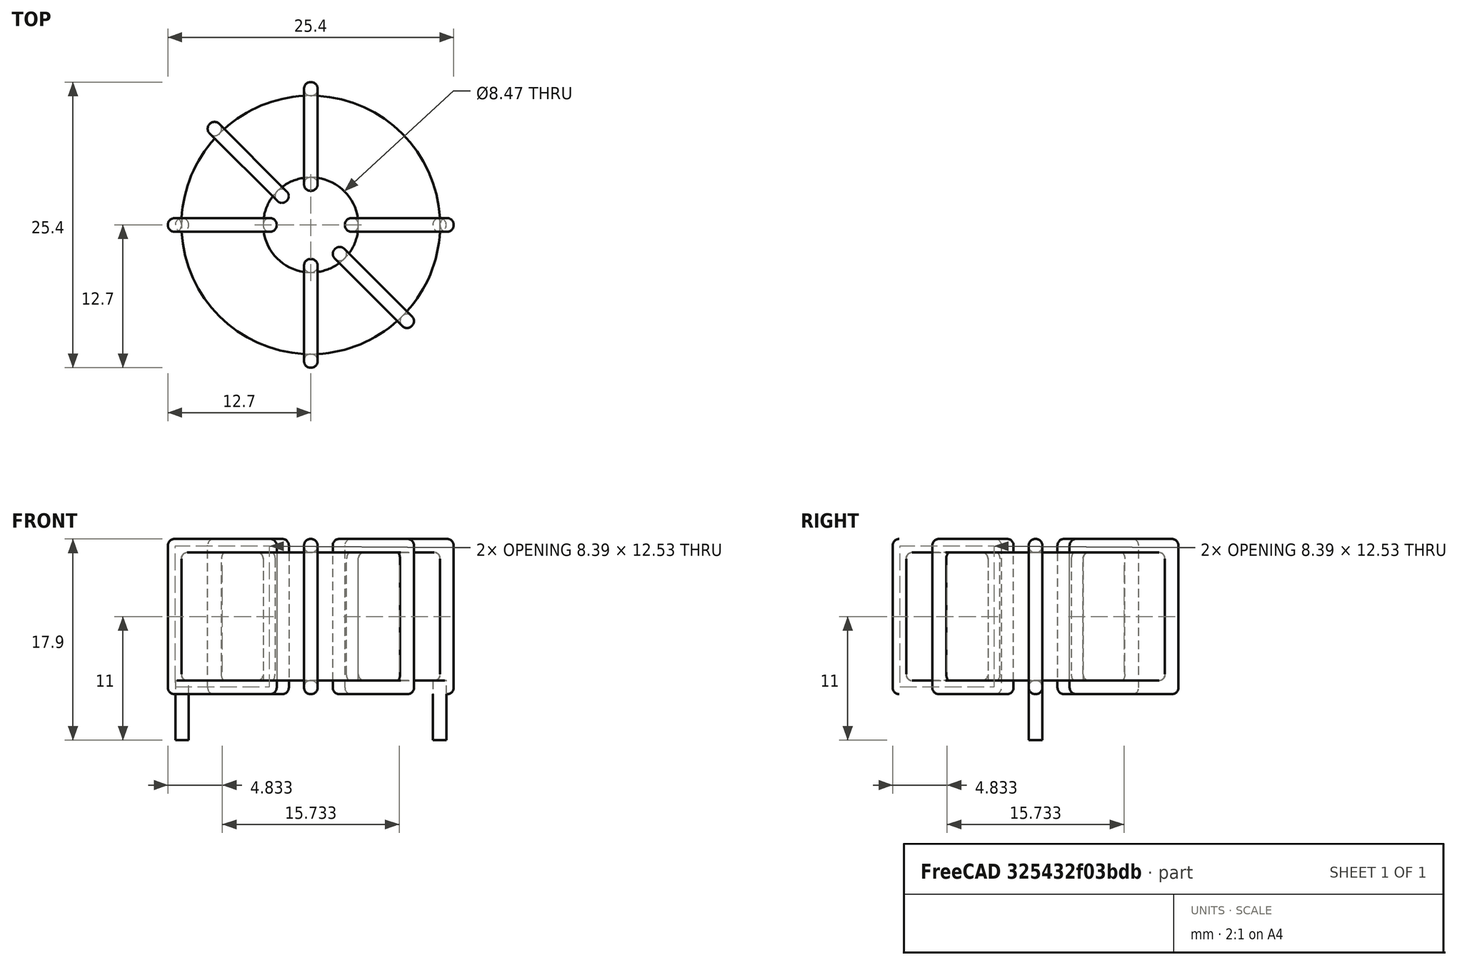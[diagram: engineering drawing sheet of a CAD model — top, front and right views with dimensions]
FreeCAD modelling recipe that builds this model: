
FCSTD DOCUMENT  (FreeCAD 0.16R6703 (Git))
Label: L_Toroid_Horizontal_D25.4mm_P22.90mm_Vishay_TJ5_BigPads
License: All rights reserved
LicenseURL: http://en.wikipedia.org/wiki/All_rights_reserved
objects: Sketcher::SketchObject×6, PartDesign::Pad×6, PartDesign::Fillet×5, Spreadsheet::Sheet×1
note: 23 computed .brp shape members not serialized (recipe doc carries the construction recipe); baked Part::Feature solids carry a one-line shape summary decoded from their .brp

FEATURE [Spreadsheet::Sheet] Spreadsheet  label="dimensions"
  cells = A1=Wx; B1(Wx)=25.4; C1(WW)=8.466666666666667; D1=25.4; A2=Wy; B2(Wy)=25.4; D2=25.4; A3=RM; B3(RMx)=22.9; C3(RMy)=0; A4=d_wire; B4(d_wire)=1.2; A5=H; B5(H)=11.4; A6=offsetx; B6(offsetx)=1.25
FEATURE [Sketcher::SketchObject] Sketch
  Placement = pos=(0,0,1.7) rot=(0,0,1;0rad)
  expr: Placement.Base.z = 0.5 + Spreadsheet.d_wire
  expr: Constraints[0] = Spreadsheet.Wx / 2 - Spreadsheet.d_wire
  expr: Constraints[4] = Spreadsheet.WW / 2
  expr: Constraints[2] = Spreadsheet.RMy / 2
  expr: Constraints[1] = Spreadsheet.RMx / 2
  sketch-geometry (2):
    g0: Circle CenterX=11.45 CenterY=0 CenterZ=0 NormalX=0 NormalY=0 NormalZ=1 Radius=11.5
    g1: Circle CenterX=11.45 CenterY=0 CenterZ=0 NormalX=0 NormalY=0 NormalZ=1 Radius=4.23333
  constraints (5):
    c: Radius(g0) = 11.5
    c: DistanceX(g-1,g0) = 11.45
    c: DistanceY(g-1,g0) = 0
    c: Coincident(g1,g0)
    c: Radius(g1) = 4.23333
FEATURE [PartDesign::Pad] Pad
  Length = 11.4
  Length2 = 100
  Placement = pos=(0,0,1.7) rot=(0,0,1;0rad)
  Sketch = -> Sketch
  Type = 0
  expr: Length = Spreadsheet.H
FEATURE [Sketcher::SketchObject] Sketch001
  Placement = pos=(0,0,1.1) rot=(0,0,1;0rad)
  expr: Placement.Base.z = 0.5 + Spreadsheet.d_wire * 0.5
  expr: Constraints[4] = Spreadsheet.RMx
  expr: Constraints[2] = Spreadsheet.RMy
  expr: Constraints[1] = Spreadsheet.d_wire / 2
  sketch-geometry (2):
    g0: Circle CenterX=0 CenterY=0 CenterZ=0 NormalX=0 NormalY=0 NormalZ=1 Radius=0.6
    g1: Circle CenterX=22.9 CenterY=0 CenterZ=0 NormalX=0 NormalY=0 NormalZ=1 Radius=0.6
  constraints (5):
    c: Equal(g0,g1)
    c: Radius(g0) = 0.6
    c: DistanceY(g-1,g1) = 0
    c: Coincident(g0,g-1)
    c: DistanceX(g-1,g1) = 22.9
FEATURE [PartDesign::Pad] Pad001
  Length = 0.6
  Length2 = 4.7
  Placement = pos=(0,0,1.1) rot=(0,0,1;0rad)
  Reversed = true
  Sketch = -> Sketch001
  Type = 4
  expr: Length2 = 3.5 + Spreadsheet.d_wire
  expr: Length = Spreadsheet.d_wire / 2
FEATURE [PartDesign::Fillet] Fillet
  Base = -> Pad [Edge6,Edge3,Edge2]
  Placement = pos=(0,0,1.7) rot=(0,0,1;0rad)
  Radius = 0.5
FEATURE [Sketcher::SketchObject] Sketch003
  Placement = pos=(11.45,0,0) rot=(1,0,0;1.5708rad)
  expr: Placement.Base.x = Spreadsheet.RMx / 2
  expr: Constraints[49] = Spreadsheet.Wx - Spreadsheet.d_wire * 2
  expr: Constraints[44] = Spreadsheet.d_wire
  expr: Constraints[23] = Spreadsheet.H
  expr: Constraints[22] = Spreadsheet.Wx / 2 - Spreadsheet.d_wire
  expr: Placement.Base.y = Spreadsheet.RMy / 2
  expr: Constraints[21] = (Spreadsheet.Wx - Spreadsheet.WW) / 2 - Spreadsheet.d_wire
  expr: Constraints[19] = Spreadsheet.d_wire
  expr: Constraints[17] = Spreadsheet.d_wire
  expr: Constraints[18] = Spreadsheet.d_wire
  expr: Constraints[16] = Spreadsheet.d_wire
  sketch-geometry (16):
    g0: LineSegment StartX=-3.03333 StartY=0.5 StartZ=0 EndX=-12.7 EndY=0.5 EndZ=0
    g1: LineSegment StartX=-12.7 StartY=0.5 StartZ=0 EndX=-12.7 EndY=14.3 EndZ=0
    g2: LineSegment StartX=-12.7 StartY=14.3 StartZ=0 EndX=-3.03333 EndY=14.3 EndZ=0
    g3: LineSegment StartX=-3.03333 StartY=14.3 StartZ=0 EndX=-3.03333 EndY=0.5 EndZ=0
    g4: LineSegment StartX=-11.5 StartY=13.1 StartZ=0 EndX=-4.23333 EndY=13.1 EndZ=0
    g5: LineSegment StartX=-4.23333 StartY=13.1 StartZ=0 EndX=-4.23333 EndY=1.7 EndZ=0
    g6: LineSegment StartX=-4.23333 StartY=1.7 StartZ=0 EndX=-11.5 EndY=1.7 EndZ=0
    g7: LineSegment StartX=-11.5 StartY=1.7 StartZ=0 EndX=-11.5 EndY=13.1 EndZ=0
    g8: LineSegment StartX=3.03333 StartY=14.3 StartZ=0 EndX=12.7 EndY=14.3 EndZ=0
    g9: LineSegment StartX=12.7 StartY=14.3 StartZ=0 EndX=12.7 EndY=0.5 EndZ=0
    g10: LineSegment StartX=12.7 StartY=0.5 StartZ=0 EndX=3.03333 EndY=0.5 EndZ=0
    g11: LineSegment StartX=3.03333 StartY=0.5 StartZ=0 EndX=3.03333 EndY=14.3 EndZ=0
    g12: LineSegment StartX=4.23333 StartY=13.1 StartZ=0 EndX=11.5 EndY=13.1 EndZ=0
    g13: LineSegment StartX=11.5 StartY=13.1 StartZ=0 EndX=11.5 EndY=1.7 EndZ=0
    g14: LineSegment StartX=11.5 StartY=1.7 StartZ=0 EndX=4.23333 EndY=1.7 EndZ=0
    g15: LineSegment StartX=4.23333 StartY=1.7 StartZ=0 EndX=4.23333 EndY=13.1 EndZ=0
  constraints (50):
    c: Horizontal(g0)
    c: Coincident(g1,g0)
    c: Vertical(g1)
    c: Coincident(g2,g1)
    c: Horizontal(g2)
    c: Coincident(g3,g2)
    c: Coincident(g3,g0)
    c: Vertical(g3)
    c: Coincident(g4,g5)
    c: Coincident(g5,g6)
    c: Coincident(g6,g7)
    c: Coincident(g7,g4)
    c: Horizontal(g4)
    c: Horizontal(g6)
    c: Vertical(g5)
    c: Vertical(g7)
    c: DistanceX(g1,g4) = 1.2
    c: DistanceY(g4,g1) = 1.2
    c: DistanceX(g5,g0) = 1.2
    c: DistanceY(g0,g5) = 1.2
    c: DistanceY(g-1,g0) = 0.5
    c: DistanceX(g6,g6) = 7.26667
    c: DistanceX(g6,g-1) = 11.5
    c: DistanceY(g7,g7) = 11.4
    c: Coincident(g8,g9)
    c: Coincident(g9,g10)
    c: Coincident(g10,g11)
    c: Coincident(g11,g8)
    c: Horizontal(g8)
    c: Horizontal(g10)
    c: Vertical(g9)
    c: Vertical(g11)
    c: Coincident(g12,g13)
    c: Coincident(g13,g14)
    c: Coincident(g14,g15)
    c: Coincident(g15,g12)
    c: Horizontal(g12)
    c: Horizontal(g14)
    c: Vertical(g13)
    c: Vertical(g15)
    c: DistanceY(g8,g2) = 0
    c: DistanceY(g10,g0) = 0
    c: DistanceY(g14,g5) = 0
    c: DistanceY(g12,g4) = 0
    c: DistanceX(g8,g12) = 1.2
    c: Equal(g8,g2)
    c: Equal(g12,g4)
    c: Equal(g9,g1)
    c: Equal(g13,g7)
    c: DistanceX(g4,g12) = 23
FEATURE [PartDesign::Pad] Pad002
  Length = 1.2
  Length2 = 100
  Midplane = true
  Placement = pos=(11.45,0,0) rot=(1,0,0;1.5708rad)
  Sketch = -> Sketch003
  Type = 0
  expr: Length = Spreadsheet.d_wire
FEATURE [PartDesign::Fillet] Fillet001
  Base = -> Pad002 [Edge38,Edge41,Edge42,Edge43,Edge29,Edge32,Edge33,Edge34,Edge25,Edge35,Edge36,Edge13,Edge14,Edge15,Edge16,Edge17,Edge18,Edge19,Edge1,Edge2,Edge3,Edge4,Edge5,Edge6,Edge7,Edge37,Edge39,Edge40,Edge20,Edge23,Edge24,Edge21,Edge22,Edge8,Edge9,Edge10,Edge11,Edge12,Edge26,Edge27,+8 more]
  Placement = pos=(11.45,0,0) rot=(1,0,0;1.5708rad)
  Radius = 0.564
  expr: Radius = Spreadsheet.d_wire * 0.47
FEATURE [Sketcher::SketchObject] Sketch004
  Placement = pos=(11.45,0,0) rot=(0.862856,0.357407,0.357407;1.71777rad)
  expr: Placement.Base.x = Spreadsheet.RMx / 2
  expr: Constraints[49] = Spreadsheet.Wx - 2 * Spreadsheet.d_wire
  expr: Constraints[44] = Spreadsheet.d_wire
  expr: Constraints[23] = Spreadsheet.H
  expr: Constraints[22] = Spreadsheet.Wx / 2 - Spreadsheet.d_wire
  expr: Placement.Base.y = Spreadsheet.RMy / 2
  expr: Constraints[21] = (Spreadsheet.Wx - Spreadsheet.WW) / 2 - Spreadsheet.d_wire
  expr: Constraints[19] = Spreadsheet.d_wire
  expr: Constraints[17] = Spreadsheet.d_wire
  expr: Constraints[18] = Spreadsheet.d_wire
  expr: Constraints[16] = Spreadsheet.d_wire
  sketch-geometry (16):
    g0: LineSegment StartX=-3.03333 StartY=0.5 StartZ=0 EndX=-12.7 EndY=0.5 EndZ=0
    g1: LineSegment StartX=-12.7 StartY=0.5 StartZ=0 EndX=-12.7 EndY=14.3 EndZ=0
    g2: LineSegment StartX=-12.7 StartY=14.3 StartZ=0 EndX=-3.03333 EndY=14.3 EndZ=0
    g3: LineSegment StartX=-3.03333 StartY=14.3 StartZ=0 EndX=-3.03333 EndY=0.5 EndZ=0
    g4: LineSegment StartX=-11.5 StartY=13.1 StartZ=0 EndX=-4.23333 EndY=13.1 EndZ=0
    g5: LineSegment StartX=-4.23333 StartY=13.1 StartZ=0 EndX=-4.23333 EndY=1.7 EndZ=0
    g6: LineSegment StartX=-4.23333 StartY=1.7 StartZ=0 EndX=-11.5 EndY=1.7 EndZ=0
    g7: LineSegment StartX=-11.5 StartY=1.7 StartZ=0 EndX=-11.5 EndY=13.1 EndZ=0
    g8: LineSegment StartX=3.03333 StartY=14.3 StartZ=0 EndX=12.7 EndY=14.3 EndZ=0
    g9: LineSegment StartX=12.7 StartY=14.3 StartZ=0 EndX=12.7 EndY=0.5 EndZ=0
    g10: LineSegment StartX=12.7 StartY=0.5 StartZ=0 EndX=3.03333 EndY=0.5 EndZ=0
    g11: LineSegment StartX=3.03333 StartY=0.5 StartZ=0 EndX=3.03333 EndY=14.3 EndZ=0
    g12: LineSegment StartX=4.23333 StartY=13.1 StartZ=0 EndX=11.5 EndY=13.1 EndZ=0
    g13: LineSegment StartX=11.5 StartY=13.1 StartZ=0 EndX=11.5 EndY=1.7 EndZ=0
    g14: LineSegment StartX=11.5 StartY=1.7 StartZ=0 EndX=4.23333 EndY=1.7 EndZ=0
    g15: LineSegment StartX=4.23333 StartY=1.7 StartZ=0 EndX=4.23333 EndY=13.1 EndZ=0
  constraints (50):
    c: Horizontal(g0)
    c: Coincident(g1,g0)
    c: Vertical(g1)
    c: Coincident(g2,g1)
    c: Horizontal(g2)
    c: Coincident(g3,g2)
    c: Coincident(g3,g0)
    c: Vertical(g3)
    c: Coincident(g4,g5)
    c: Coincident(g5,g6)
    c: Coincident(g6,g7)
    c: Coincident(g7,g4)
    c: Horizontal(g4)
    c: Horizontal(g6)
    c: Vertical(g5)
    c: Vertical(g7)
    c: DistanceX(g1,g4) = 1.2
    c: DistanceY(g4,g1) = 1.2
    c: DistanceX(g5,g0) = 1.2
    c: DistanceY(g0,g5) = 1.2
    c: DistanceY(g-1,g0) = 0.5
    c: DistanceX(g6,g6) = 7.26667
    c: DistanceX(g6,g-1) = 11.5
    c: DistanceY(g7,g7) = 11.4
    c: Coincident(g8,g9)
    c: Coincident(g9,g10)
    c: Coincident(g10,g11)
    c: Coincident(g11,g8)
    c: Horizontal(g8)
    c: Horizontal(g10)
    c: Vertical(g9)
    c: Vertical(g11)
    c: Coincident(g12,g13)
    c: Coincident(g13,g14)
    c: Coincident(g14,g15)
    c: Coincident(g15,g12)
    c: Horizontal(g12)
    c: Horizontal(g14)
    c: Vertical(g13)
    c: Vertical(g15)
    c: DistanceY(g8,g2) = 0
    c: DistanceY(g10,g0) = 0
    c: DistanceY(g14,g5) = 0
    c: DistanceY(g12,g4) = 0
    c: DistanceX(g8,g12) = 1.2
    c: Equal(g8,g2)
    c: Equal(g12,g4)
    c: Equal(g9,g1)
    c: Equal(g13,g7)
    c: DistanceX(g4,g12) = 23
FEATURE [PartDesign::Pad] Pad003
  Length = 1.2
  Length2 = 100
  Midplane = true
  Placement = pos=(11.45,0,0) rot=(0.862856,0.357407,0.357407;1.71777rad)
  Sketch = -> Sketch004
  Type = 0
  expr: Length = Spreadsheet.d_wire
FEATURE [PartDesign::Fillet] Fillet002
  Base = -> Pad003 [Edge38,Edge41,Edge42,Edge43,Edge29,Edge32,Edge33,Edge34,Edge25,Edge35,Edge36,Edge13,Edge14,Edge15,Edge16,Edge17,Edge18,Edge19,Edge1,Edge2,Edge3,Edge4,Edge5,Edge6,Edge7,Edge37,Edge39,Edge40,Edge20,Edge23,Edge24,Edge21,Edge22,Edge8,Edge9,Edge10,Edge11,Edge12,Edge26,Edge27,+8 more]
  Placement = pos=(11.45,0,0) rot=(0.862856,0.357407,0.357407;1.71777rad)
  Radius = 0.564
  expr: Radius = Spreadsheet.d_wire * 0.47
FEATURE [Sketcher::SketchObject] Sketch005
  Placement = pos=(11.45,0,0) rot=(0.862856,-0.357407,-0.357407;1.71777rad)
  expr: Placement.Base.x = Spreadsheet.RMx / 2
  expr: Constraints[49] = Spreadsheet.Wx - 2 * Spreadsheet.d_wire
  expr: Constraints[44] = Spreadsheet.d_wire
  expr: Constraints[23] = Spreadsheet.H
  expr: Constraints[22] = Spreadsheet.Wx / 2 - Spreadsheet.d_wire
  expr: Placement.Base.y = Spreadsheet.RMy / 2
  expr: Constraints[21] = (Spreadsheet.Wx - Spreadsheet.WW) / 2 - Spreadsheet.d_wire
  expr: Constraints[19] = Spreadsheet.d_wire
  expr: Constraints[17] = Spreadsheet.d_wire
  expr: Constraints[18] = Spreadsheet.d_wire
  expr: Constraints[16] = Spreadsheet.d_wire
  sketch-geometry (16):
    g0: LineSegment StartX=-3.03333 StartY=0.5 StartZ=0 EndX=-12.7 EndY=0.5 EndZ=0
    g1: LineSegment StartX=-12.7 StartY=0.5 StartZ=0 EndX=-12.7 EndY=14.3 EndZ=0
    g2: LineSegment StartX=-12.7 StartY=14.3 StartZ=0 EndX=-3.03333 EndY=14.3 EndZ=0
    g3: LineSegment StartX=-3.03333 StartY=14.3 StartZ=0 EndX=-3.03333 EndY=0.5 EndZ=0
    g4: LineSegment StartX=-11.5 StartY=13.1 StartZ=0 EndX=-4.23333 EndY=13.1 EndZ=0
    g5: LineSegment StartX=-4.23333 StartY=13.1 StartZ=0 EndX=-4.23333 EndY=1.7 EndZ=0
    g6: LineSegment StartX=-4.23333 StartY=1.7 StartZ=0 EndX=-11.5 EndY=1.7 EndZ=0
    g7: LineSegment StartX=-11.5 StartY=1.7 StartZ=0 EndX=-11.5 EndY=13.1 EndZ=0
    g8: LineSegment StartX=3.03333 StartY=14.3 StartZ=0 EndX=12.7 EndY=14.3 EndZ=0
    g9: LineSegment StartX=12.7 StartY=14.3 StartZ=0 EndX=12.7 EndY=0.5 EndZ=0
    g10: LineSegment StartX=12.7 StartY=0.5 StartZ=0 EndX=3.03333 EndY=0.5 EndZ=0
    g11: LineSegment StartX=3.03333 StartY=0.5 StartZ=0 EndX=3.03333 EndY=14.3 EndZ=0
    g12: LineSegment StartX=4.23333 StartY=13.1 StartZ=0 EndX=11.5 EndY=13.1 EndZ=0
    g13: LineSegment StartX=11.5 StartY=13.1 StartZ=0 EndX=11.5 EndY=1.7 EndZ=0
    g14: LineSegment StartX=11.5 StartY=1.7 StartZ=0 EndX=4.23333 EndY=1.7 EndZ=0
    g15: LineSegment StartX=4.23333 StartY=1.7 StartZ=0 EndX=4.23333 EndY=13.1 EndZ=0
  constraints (50):
    c: Horizontal(g0)
    c: Coincident(g1,g0)
    c: Vertical(g1)
    c: Coincident(g2,g1)
    c: Horizontal(g2)
    c: Coincident(g3,g2)
    c: Coincident(g3,g0)
    c: Vertical(g3)
    c: Coincident(g4,g5)
    c: Coincident(g5,g6)
    c: Coincident(g6,g7)
    c: Coincident(g7,g4)
    c: Horizontal(g4)
    c: Horizontal(g6)
    c: Vertical(g5)
    c: Vertical(g7)
    c: DistanceX(g1,g4) = 1.2
    c: DistanceY(g4,g1) = 1.2
    c: DistanceX(g5,g0) = 1.2
    c: DistanceY(g0,g5) = 1.2
    c: DistanceY(g-1,g0) = 0.5
    c: DistanceX(g6,g6) = 7.26667
    c: DistanceX(g6,g-1) = 11.5
    c: DistanceY(g7,g7) = 11.4
    c: Coincident(g8,g9)
    c: Coincident(g9,g10)
    c: Coincident(g10,g11)
    c: Coincident(g11,g8)
    c: Horizontal(g8)
    c: Horizontal(g10)
    c: Vertical(g9)
    c: Vertical(g11)
    c: Coincident(g12,g13)
    c: Coincident(g13,g14)
    c: Coincident(g14,g15)
    c: Coincident(g15,g12)
    c: Horizontal(g12)
    c: Horizontal(g14)
    c: Vertical(g13)
    c: Vertical(g15)
    c: DistanceY(g8,g2) = 0
    c: DistanceY(g10,g0) = 0
    c: DistanceY(g14,g5) = 0
    c: DistanceY(g12,g4) = 0
    c: DistanceX(g8,g12) = 1.2
    c: Equal(g8,g2)
    c: Equal(g12,g4)
    c: Equal(g9,g1)
    c: Equal(g13,g7)
    c: DistanceX(g4,g12) = 23
FEATURE [PartDesign::Pad] Pad004
  Length = 1.2
  Length2 = 100
  Midplane = true
  Placement = pos=(11.45,0,0) rot=(0.862856,-0.357407,-0.357407;1.71777rad)
  Sketch = -> Sketch005
  Type = 0
  expr: Length = Spreadsheet.d_wire
FEATURE [PartDesign::Fillet] Fillet003
  Base = -> Pad004 [Edge38,Edge41,Edge42,Edge43,Edge29,Edge32,Edge33,Edge34,Edge25,Edge35,Edge36,Edge13,Edge14,Edge15,Edge16,Edge17,Edge18,Edge19,Edge1,Edge2,Edge3,Edge4,Edge5,Edge6,Edge7,Edge37,Edge39,Edge40,Edge20,Edge23,Edge24,Edge21,Edge22,Edge8,Edge9,Edge10,Edge11,Edge12,Edge26,Edge27,+8 more]
  Placement = pos=(11.45,0,0) rot=(0.862856,-0.357407,-0.357407;1.71777rad)
  Radius = 0.564
  expr: Radius = Spreadsheet.d_wire * 0.47
FEATURE [Sketcher::SketchObject] Sketch006
  Placement = pos=(11.45,0,0) rot=(0.57735,0.57735,0.57735;2.0944rad)
  expr: Placement.Base.x = Spreadsheet.RMx / 2
  expr: Constraints[49] = Spreadsheet.Wx - Spreadsheet.d_wire * 2
  expr: Constraints[44] = Spreadsheet.d_wire
  expr: Constraints[23] = Spreadsheet.H
  expr: Constraints[22] = Spreadsheet.Wx / 2 - Spreadsheet.d_wire
  expr: Placement.Base.y = Spreadsheet.RMy / 2
  expr: Constraints[21] = (Spreadsheet.Wx - Spreadsheet.WW) / 2 - Spreadsheet.d_wire
  expr: Constraints[19] = Spreadsheet.d_wire
  expr: Constraints[17] = Spreadsheet.d_wire
  expr: Constraints[18] = Spreadsheet.d_wire
  expr: Constraints[16] = Spreadsheet.d_wire
  sketch-geometry (16):
    g0: LineSegment StartX=-3.03333 StartY=0.5 StartZ=0 EndX=-12.7 EndY=0.5 EndZ=0
    g1: LineSegment StartX=-12.7 StartY=0.5 StartZ=0 EndX=-12.7 EndY=14.3 EndZ=0
    g2: LineSegment StartX=-12.7 StartY=14.3 StartZ=0 EndX=-3.03333 EndY=14.3 EndZ=0
    g3: LineSegment StartX=-3.03333 StartY=14.3 StartZ=0 EndX=-3.03333 EndY=0.5 EndZ=0
    g4: LineSegment StartX=-11.5 StartY=13.1 StartZ=0 EndX=-4.23333 EndY=13.1 EndZ=0
    g5: LineSegment StartX=-4.23333 StartY=13.1 StartZ=0 EndX=-4.23333 EndY=1.7 EndZ=0
    g6: LineSegment StartX=-4.23333 StartY=1.7 StartZ=0 EndX=-11.5 EndY=1.7 EndZ=0
    g7: LineSegment StartX=-11.5 StartY=1.7 StartZ=0 EndX=-11.5 EndY=13.1 EndZ=0
    g8: LineSegment StartX=3.03333 StartY=14.3 StartZ=0 EndX=12.7 EndY=14.3 EndZ=0
    g9: LineSegment StartX=12.7 StartY=14.3 StartZ=0 EndX=12.7 EndY=0.5 EndZ=0
    g10: LineSegment StartX=12.7 StartY=0.5 StartZ=0 EndX=3.03333 EndY=0.5 EndZ=0
    g11: LineSegment StartX=3.03333 StartY=0.5 StartZ=0 EndX=3.03333 EndY=14.3 EndZ=0
    g12: LineSegment StartX=4.23333 StartY=13.1 StartZ=0 EndX=11.5 EndY=13.1 EndZ=0
    g13: LineSegment StartX=11.5 StartY=13.1 StartZ=0 EndX=11.5 EndY=1.7 EndZ=0
    g14: LineSegment StartX=11.5 StartY=1.7 StartZ=0 EndX=4.23333 EndY=1.7 EndZ=0
    g15: LineSegment StartX=4.23333 StartY=1.7 StartZ=0 EndX=4.23333 EndY=13.1 EndZ=0
  constraints (50):
    c: Horizontal(g0)
    c: Coincident(g1,g0)
    c: Vertical(g1)
    c: Coincident(g2,g1)
    c: Horizontal(g2)
    c: Coincident(g3,g2)
    c: Coincident(g3,g0)
    c: Vertical(g3)
    c: Coincident(g4,g5)
    c: Coincident(g5,g6)
    c: Coincident(g6,g7)
    c: Coincident(g7,g4)
    c: Horizontal(g4)
    c: Horizontal(g6)
    c: Vertical(g5)
    c: Vertical(g7)
    c: DistanceX(g1,g4) = 1.2
    c: DistanceY(g4,g1) = 1.2
    c: DistanceX(g5,g0) = 1.2
    c: DistanceY(g0,g5) = 1.2
    c: DistanceY(g-1,g0) = 0.5
    c: DistanceX(g6,g6) = 7.26667
    c: DistanceX(g6,g-1) = 11.5
    c: DistanceY(g7,g7) = 11.4
    c: Coincident(g8,g9)
    c: Coincident(g9,g10)
    c: Coincident(g10,g11)
    c: Coincident(g11,g8)
    c: Horizontal(g8)
    c: Horizontal(g10)
    c: Vertical(g9)
    c: Vertical(g11)
    c: Coincident(g12,g13)
    c: Coincident(g13,g14)
    c: Coincident(g14,g15)
    c: Coincident(g15,g12)
    c: Horizontal(g12)
    c: Horizontal(g14)
    c: Vertical(g13)
    c: Vertical(g15)
    c: DistanceY(g8,g2) = 0
    c: DistanceY(g10,g0) = 0
    c: DistanceY(g14,g5) = 0
    c: DistanceY(g12,g4) = 0
    c: DistanceX(g8,g12) = 1.2
    c: Equal(g8,g2)
    c: Equal(g12,g4)
    c: Equal(g9,g1)
    c: Equal(g13,g7)
    c: DistanceX(g4,g12) = 23
FEATURE [PartDesign::Pad] Pad005
  Length = 1.2
  Length2 = 100
  Midplane = true
  Placement = pos=(11.45,0,0) rot=(0.57735,0.57735,0.57735;2.0944rad)
  Sketch = -> Sketch006
  Type = 0
  expr: Length = Spreadsheet.d_wire
FEATURE [PartDesign::Fillet] Fillet004
  Base = -> Pad005 [Edge38,Edge41,Edge42,Edge43,Edge29,Edge32,Edge33,Edge34,Edge25,Edge35,Edge36,Edge13,Edge14,Edge15,Edge16,Edge17,Edge18,Edge19,Edge1,Edge2,Edge3,Edge4,Edge5,Edge6,Edge7,Edge37,Edge39,Edge40,Edge20,Edge23,Edge24,Edge21,Edge22,Edge8,Edge9,Edge10,Edge11,Edge12,Edge26,Edge27,+8 more]
  Placement = pos=(11.45,0,0) rot=(0.57735,0.57735,0.57735;2.0944rad)
  Radius = 0.564
  expr: Radius = Spreadsheet.d_wire * 0.47
